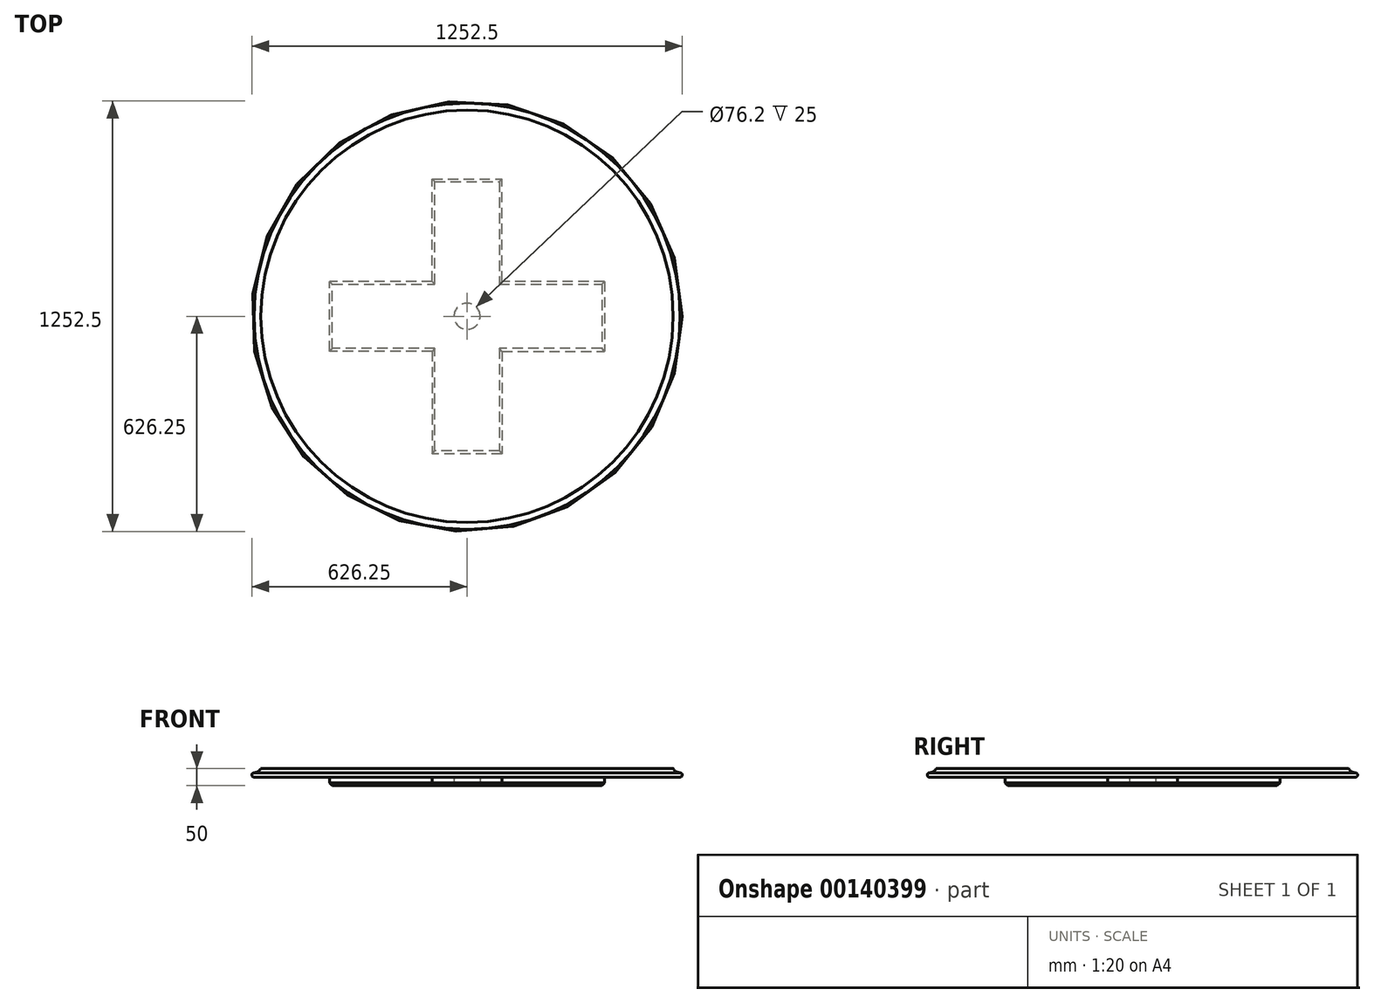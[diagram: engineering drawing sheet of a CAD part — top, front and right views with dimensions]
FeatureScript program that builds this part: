
annotation { "Feature Type Name" : "Feature", "Feature Type Description" : "" }
export const myFeature = defineFeature(function(context is Context, id is Id, definition is map)
    precondition{}
    {
        {
            var Q0;
            Q0=qCreatedBy(makeId("Top.planeOp"),FACE);
            var sketch = newSketch(context, id + "F0", { "sketchPlane" : qUnion([Q0])});
            skCircle(sketch, "E0", {"center": v(0, 0) * mm, "radius": 600.08 * mm});
            skSolve(sketch);
        }
        {
            var Q0;
            Q0=makeQuery(id+"F0.imprint","IMPRINT",FACE,{"disambiguationData":[TD([[makeQuery(id+"F0.imprint","IMPRINT",EDGE,{"derivedFrom":sQuery(id+"F0.wireOp",EDGE,"E0")}),1.0]])]});
            extrude(context, id + "F1", {"entities" : qUnion([Q0]), "depth" : 25 * mm});
        }
        {
            var Q0;
            Q0=qCreatedBy(makeId("Front.planeOp"),FACE);
            var sketch = newSketch(context, id + "F2", { "sketchPlane" : qUnion([Q0])});
            skLineSegment(sketch, "E1.bottom", {"start": v(600, 0) * mm, "end": v(620, 0) * mm});
            skLineSegment(sketch, "E1.left", {"start": v(600, 0) * mm, "end": v(600, 25) * mm});
            skArc(sketch, "E2", {"start": v(620, 0) * mm, "mid": v(626.25, 6.25) * mm, "end": v(620, 12.5) * mm});
            skArc(sketch, "E3", {"start": v(600, 25) * mm, "mid": v(608.43, 16.24) * mm, "end": v(620, 12.5) * mm});
            skSolve(sketch);
        }
        {
            var Q0;
            Q0=makeQuery(id+"F2.imprint","IMPRINT",FACE,{"disambiguationData":[TD([[makeQuery(id+"F2.imprint","IMPRINT",EDGE,{"derivedFrom":sQuery(id+"F2.wireOp",EDGE,"E1.bottom")}),1.0]])]});
            var Q1;
            Q1=makeQuery(id+"F1.opExtrude","CAP_EDGE",EDGE,{"disambiguationData":[OSD([sQuery(id+"F0.wireOp",EDGE,"E0")])],"isStart":true});
            sweep(context, id + "F3", {"operationType" : NewBodyOperationType.ADD, "profiles" : qUnion([Q0]), "path" : qUnion([Q1])});
        }
        {
            var Q0;
            {var subQ0=sQuery(id+"F0.wireOp",EDGE,"E0");Q0=makeQuery(id+"F3.boolean.opBoolean","MERGE",FACE,{"derivedFrom":[makeQuery(id+"F1.opExtrude","CAP_FACE",FACE,{"disambiguationData":[OSD([subQ0])],"isStart":true}),makeQuery(id+"F3.opSweep","SWEPT_FACE",FACE,{"disambiguationData":[OSD([subQ0,sQuery(id+"F2.wireOp",EDGE,"E1.bottom")])]})]});}
            var sketch = newSketch(context, id + "F4", { "sketchPlane" : qUnion([Q0])});
            skLineSegment(sketch, "E4", {"start": v(464.31, 0) * mm, "end": v(-486.66, 0) * mm, "construction": true});
            skLineSegment(sketch, "E5", {"start": v(0, 394.2) * mm, "end": v(0, -377.95) * mm, "construction": true});
            skLineSegment(sketch, "E6", {"start": v(400, 101.6) * mm, "end": v(0, 101.6) * mm});
            skLineSegment(sketch, "E7", {"start": v(400, 101.6) * mm, "end": v(400, 0) * mm});
            skLineSegment(sketch, "E8.MirrorCS", {"start": v(400, -101.6) * mm, "end": v(400, 0) * mm});
            skLineSegment(sketch, "E9.MirrorCS", {"start": v(400, -101.6) * mm, "end": v(0, -101.6) * mm});
            skLineSegment(sketch, "E10.MirrorCS", {"start": v(-400, 101.6) * mm, "end": v(0, 101.6) * mm});
            skLineSegment(sketch, "E11.MirrorCS", {"start": v(-400, 101.6) * mm, "end": v(-400, 0) * mm});
            skLineSegment(sketch, "E12.MirrorCS", {"start": v(-400, -101.6) * mm, "end": v(-400, 0) * mm});
            skLineSegment(sketch, "E13.MirrorCS", {"start": v(-400, -101.6) * mm, "end": v(0, -101.6) * mm});
            skLineSegment(sketch, "E14", {"start": v(101.6, 101.6) * mm, "end": v(101.6, 400) * mm});
            skLineSegment(sketch, "E15", {"start": v(101.6, 400) * mm, "end": v(0, 400) * mm});
            skLineSegment(sketch, "E16.MirrorCS", {"start": v(101.6, -101.6) * mm, "end": v(101.6, -400) * mm});
            skLineSegment(sketch, "E17.MirrorCS", {"start": v(101.6, -400) * mm, "end": v(0, -400) * mm});
            skLineSegment(sketch, "E18.MirrorCS", {"start": v(-101.6, 400) * mm, "end": v(0, 400) * mm});
            skLineSegment(sketch, "E19.MirrorCS", {"start": v(-101.6, 101.6) * mm, "end": v(-101.6, 400) * mm});
            skLineSegment(sketch, "E20.MirrorCS", {"start": v(-101.6, -101.6) * mm, "end": v(-101.6, -400) * mm});
            skLineSegment(sketch, "E21.MirrorCS", {"start": v(-101.6, -400) * mm, "end": v(0, -400) * mm});
            skSolve(sketch);
        }
        {
            var Q0;
            {var subQ10=sQuery(id+"F4.wireOp",EDGE,"E7");Q0=makeQuery(id+"F4.imprint","IMPRINT",FACE,{"disambiguationData":[TD([[makeQuery(id+"F4.imprint","IMPRINT",EDGE,{"derivedFrom":subQ10}),-1.0]])]});}
            extrude(context, id + "F5", {"entities" : qUnion([Q0]), "operationType" : NewBodyOperationType.ADD, "depth" : 25 * mm});
        }
        {
            var Q0;
            {var subQ0=sQuery(id+"F4.wireOp",EDGE,"E14");Q0=makeQuery(id+"F4.imprint","IMPRINT",FACE,{"disambiguationData":[TD([[makeQuery(id+"F4.imprint","IMPRINT",EDGE,{"derivedFrom":subQ0}),1.0]])]});}
            var Q1;
            {var subQ0=sQuery(id+"F4.wireOp",EDGE,"E16.MirrorCS");Q1=makeQuery(id+"F4.imprint","IMPRINT",FACE,{"disambiguationData":[TD([[makeQuery(id+"F4.imprint","IMPRINT",EDGE,{"derivedFrom":subQ0}),-1.0]])]});}
            extrude(context, id + "F6", {"entities" : qUnion([Q0, Q1]), "operationType" : NewBodyOperationType.ADD, "depth" : 25 * mm});
        }
        {
            var Q0;
            {var subQ4=sQuery(id+"F4.wireOp",EDGE,"E20.MirrorCS");var subQ5=sQuery(id+"F4.wireOp",EDGE,"E13.MirrorCS");var subQ6=sQuery(id+"F4.wireOp",EDGE,"E9.MirrorCS");Q0=makeQuery(id+"F6.boolean.opBoolean","SPLIT",EDGE,{"disambiguationData":[TD([makeQuery(id+"F6.opExtrude","SWEPT_FACE",FACE,{"disambiguationData":[OSD([subQ4])]})])],"derivedFrom":makeQuery(id+"F5.opExtrude","CAP_EDGE",EDGE,{"disambiguationData":[OSD([subQ6,subQ5])],"isStart":false})});}
            var Q1;
            Q1=makeQuery(id+"F5.opExtrude","CAP_EDGE",EDGE,{"disambiguationData":[OSD([sQuery(id+"F4.wireOp",EDGE,"E11.MirrorCS"),sQuery(id+"F4.wireOp",EDGE,"E12.MirrorCS")])],"isStart":false});
            var Q2;
            {var subQ0=sQuery(id+"F4.wireOp",EDGE,"E10.MirrorCS");var subQ1=sQuery(id+"F4.wireOp",EDGE,"E6");var subQ6=sQuery(id+"F4.wireOp",EDGE,"E19.MirrorCS");Q2=makeQuery(id+"F6.boolean.opBoolean","SPLIT",EDGE,{"disambiguationData":[TD([makeQuery(id+"F6.opExtrude","SWEPT_FACE",FACE,{"disambiguationData":[OSD([subQ6])]})])],"derivedFrom":makeQuery(id+"F5.opExtrude","CAP_EDGE",EDGE,{"disambiguationData":[OSD([subQ1,subQ0])],"isStart":false})});}
            var Q3;
            Q3=makeQuery(id+"F6.opExtrude","CAP_EDGE",EDGE,{"disambiguationData":[OSD([sQuery(id+"F4.wireOp",EDGE,"E19.MirrorCS")])],"isStart":false});
            var Q4;
            Q4=makeQuery(id+"F6.opExtrude","CAP_EDGE",EDGE,{"disambiguationData":[OSD([sQuery(id+"F4.wireOp",EDGE,"E15"),sQuery(id+"F4.wireOp",EDGE,"E18.MirrorCS")])],"isStart":false});
            var Q5;
            Q5=makeQuery(id+"F6.opExtrude","CAP_EDGE",EDGE,{"disambiguationData":[OSD([sQuery(id+"F4.wireOp",EDGE,"E14")])],"isStart":false});
            var Q6;
            {var subQ2=sQuery(id+"F4.wireOp",EDGE,"E10.MirrorCS");var subQ3=sQuery(id+"F4.wireOp",EDGE,"E6");var subQ6=sQuery(id+"F4.wireOp",EDGE,"E14");Q6=makeQuery(id+"F6.boolean.opBoolean","SPLIT",EDGE,{"disambiguationData":[TD([makeQuery(id+"F6.opExtrude","SWEPT_FACE",FACE,{"disambiguationData":[OSD([subQ6])]})])],"derivedFrom":makeQuery(id+"F5.opExtrude","CAP_EDGE",EDGE,{"disambiguationData":[OSD([subQ3,subQ2])],"isStart":false})});}
            var Q7;
            Q7=makeQuery(id+"F5.opExtrude","CAP_EDGE",EDGE,{"disambiguationData":[OSD([sQuery(id+"F4.wireOp",EDGE,"E7"),sQuery(id+"F4.wireOp",EDGE,"E8.MirrorCS")])],"isStart":false});
            var Q8;
            {var subQ2=sQuery(id+"F4.wireOp",EDGE,"E16.MirrorCS");var subQ5=sQuery(id+"F4.wireOp",EDGE,"E13.MirrorCS");var subQ6=sQuery(id+"F4.wireOp",EDGE,"E9.MirrorCS");Q8=makeQuery(id+"F6.boolean.opBoolean","SPLIT",EDGE,{"disambiguationData":[TD([makeQuery(id+"F6.opExtrude","SWEPT_FACE",FACE,{"disambiguationData":[OSD([subQ2])]})])],"derivedFrom":makeQuery(id+"F5.opExtrude","CAP_EDGE",EDGE,{"disambiguationData":[OSD([subQ6,subQ5])],"isStart":false})});}
            var Q9;
            Q9=makeQuery(id+"F6.opExtrude","CAP_EDGE",EDGE,{"disambiguationData":[OSD([sQuery(id+"F4.wireOp",EDGE,"E16.MirrorCS")])],"isStart":false});
            var Q10;
            Q10=makeQuery(id+"F6.opExtrude","CAP_EDGE",EDGE,{"disambiguationData":[OSD([sQuery(id+"F4.wireOp",EDGE,"E17.MirrorCS"),sQuery(id+"F4.wireOp",EDGE,"E21.MirrorCS")])],"isStart":false});
            var Q11;
            Q11=makeQuery(id+"F6.opExtrude","CAP_EDGE",EDGE,{"disambiguationData":[OSD([sQuery(id+"F4.wireOp",EDGE,"E20.MirrorCS")])],"isStart":false});
            chamfer(context, id + "F7", {"entities" : qUnion([Q0, Q1, Q2, Q3, Q4, Q5, Q6, Q7, Q8, Q9, Q10, Q11]), "width" : 8 * mm, "tangentPropagation" : true});
        }
        {
            var Q0;
            {var subQ0=sQuery(id+"F4.wireOp",EDGE,"E13.MirrorCS");var subQ1=sQuery(id+"F4.wireOp",EDGE,"E9.MirrorCS");var subQ2=sQuery(id+"F4.wireOp",EDGE,"E10.MirrorCS");var subQ3=sQuery(id+"F4.wireOp",EDGE,"E6");Q0=makeQuery(id+"F6.boolean.opBoolean","MERGE",FACE,{"derivedFrom":[makeQuery(id+"F5.opExtrude","CAP_FACE",FACE,{"disambiguationData":[OSD([subQ3,sQuery(id+"F4.wireOp",EDGE,"E7"),sQuery(id+"F4.wireOp",EDGE,"E8.MirrorCS"),subQ1,subQ2,sQuery(id+"F4.wireOp",EDGE,"E11.MirrorCS"),sQuery(id+"F4.wireOp",EDGE,"E12.MirrorCS"),subQ0])],"isStart":false}),makeQuery(id+"F6.opExtrude","CAP_FACE",FACE,{"disambiguationData":[OSD([subQ3,subQ2,sQuery(id+"F4.wireOp",EDGE,"E14"),sQuery(id+"F4.wireOp",EDGE,"E15"),sQuery(id+"F4.wireOp",EDGE,"E18.MirrorCS"),sQuery(id+"F4.wireOp",EDGE,"E19.MirrorCS")])],"isStart":false}),makeQuery(id+"F6.opExtrude","CAP_FACE",FACE,{"disambiguationData":[OSD([subQ1,subQ0,sQuery(id+"F4.wireOp",EDGE,"E16.MirrorCS"),sQuery(id+"F4.wireOp",EDGE,"E17.MirrorCS"),sQuery(id+"F4.wireOp",EDGE,"E20.MirrorCS"),sQuery(id+"F4.wireOp",EDGE,"E21.MirrorCS")])],"isStart":false})]});}
            var sketch = newSketch(context, id + "F8", { "sketchPlane" : qUnion([Q0])});
            skCircle(sketch, "E22", {"center": v(0, 0) * mm, "radius": 38.1 * mm});
            skSolve(sketch);
        }
        {
            var Q0;
            Q0=makeQuery(id+"F8.imprint","IMPRINT",FACE,{"disambiguationData":[TD([[makeQuery(id+"F8.imprint","IMPRINT",EDGE,{"derivedFrom":sQuery(id+"F8.wireOp",EDGE,"E22")}),1.0]])]});
            extrude(context, id + "F9", {"entities" : qUnion([Q0]), "operationType" : NewBodyOperationType.REMOVE, "oppositeDirection" : true, "depth" : 25 * mm});
        }
    });
